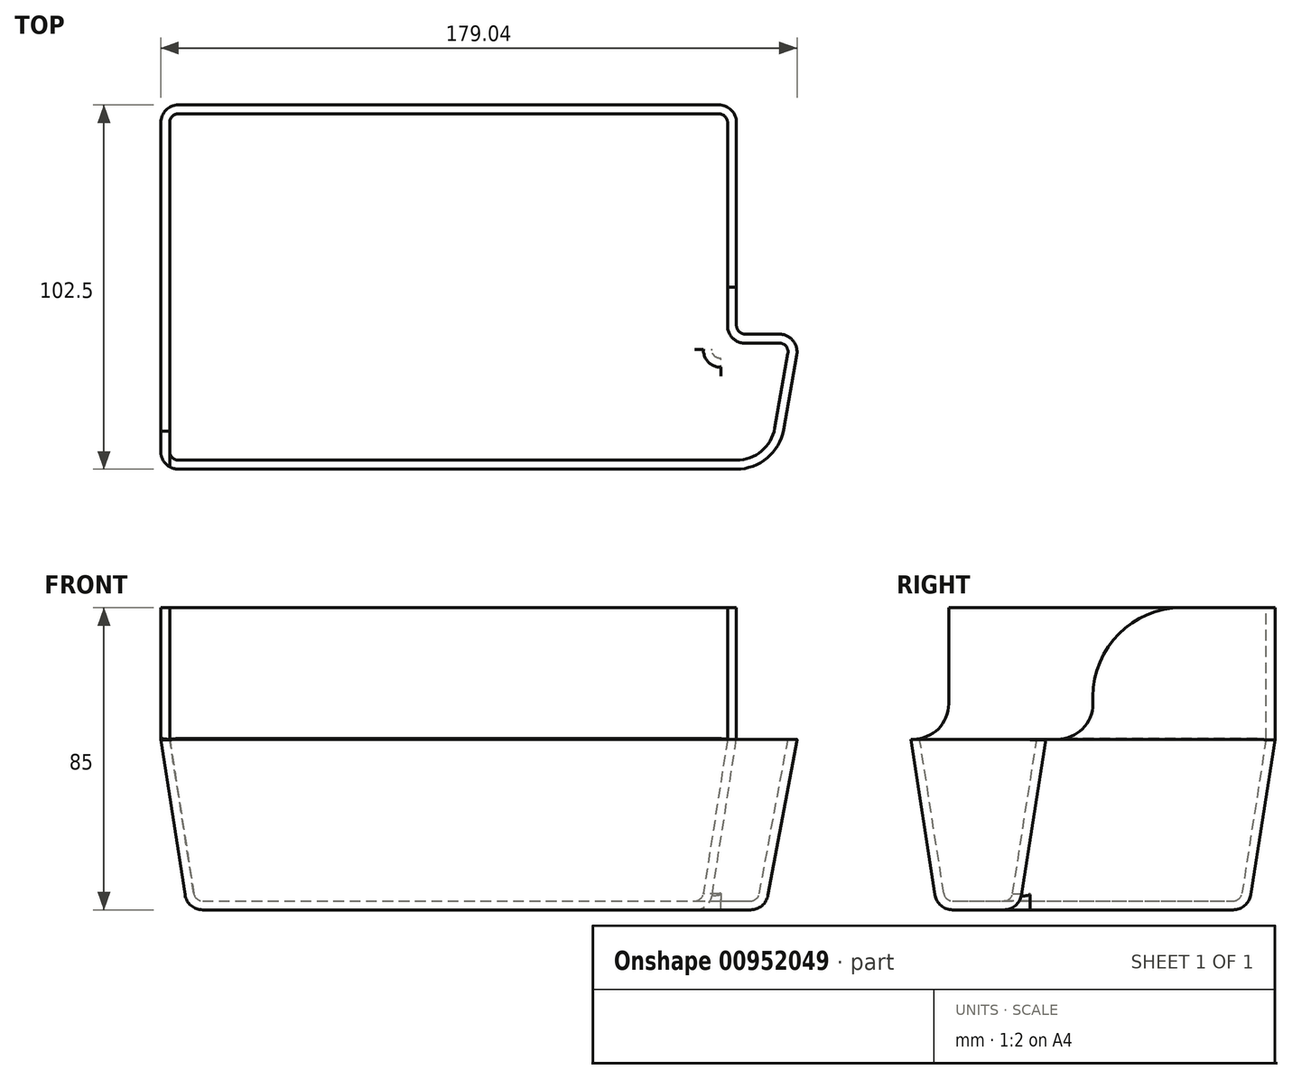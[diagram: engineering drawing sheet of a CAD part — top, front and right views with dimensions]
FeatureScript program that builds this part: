
annotation { "Feature Type Name" : "Feature", "Feature Type Description" : "" }
export const myFeature = defineFeature(function(context is Context, id is Id, definition is map)
    precondition{}
    {
        {
            var Q0;
            Q0=qCreatedBy(makeId("Top.planeOp"),FACE);
            var sketch = newSketch(context, id + "F0", { "sketchPlane" : qUnion([Q0])});
            skLineSegment(sketch, "E0.bottom", {"start": v(-81, -51.25) * mm, "end": v(81, -51.25) * mm});
            skLineSegment(sketch, "E0.top", {"start": v(-81, 51.25) * mm, "end": v(81, 51.25) * mm});
            skLineSegment(sketch, "E0.left", {"start": v(-81, -51.25) * mm, "end": v(-81, 51.25) * mm});
            skLineSegment(sketch, "E0.right", {"start": v(81, -13.25) * mm, "end": v(81, 51.25) * mm});
            skPoint(sketch, "E0.middle", {"position": v(0, 0) * mm});
            skLineSegment(sketch, "E1", {"start": v(81, -13.25) * mm, "end": v(99, -13.25) * mm});
            skLineSegment(sketch, "E2", {"start": v(99, -13.25) * mm, "end": v(94.26, -40.12) * mm});
            skArc(sketch, "E3", {"start": v(81, -51.25) * mm, "mid": v(89.66, -48.1) * mm, "end": v(94.26, -40.12) * mm});
            skSolve(sketch);
        }
        {
            var Q0;
            Q0 = qSketchRegion(id + "F0", true);
            extrude(context, id + "F1", {"entities" : qUnion([Q0]), "depth" : 85 * mm, "offsetDistance" : 25 * mm});
        }
        {
            var Q0;
            Q0=makeQuery(id+"F1.opExtrude","CAP_EDGE",EDGE,{"disambiguationData":[OSD([sQuery(id+"F0.wireOp",EDGE,"E0.bottom")])],"isStart":true});
            var Q1;
            Q1=makeQuery(id+"F1.opExtrude","CAP_EDGE",EDGE,{"disambiguationData":[OSD([sQuery(id+"F0.wireOp",EDGE,"E1")])],"isStart":true});
            var Q2;
            Q2=makeQuery(id+"F1.opExtrude","CAP_EDGE",EDGE,{"disambiguationData":[OSD([sQuery(id+"F0.wireOp",EDGE,"E0.right")])],"isStart":true});
            var Q3;
            Q3=makeQuery(id+"F1.opExtrude","CAP_EDGE",EDGE,{"disambiguationData":[OSD([sQuery(id+"F0.wireOp",EDGE,"E0.top")])],"isStart":true});
            var Q4;
            Q4=makeQuery(id+"F1.opExtrude","CAP_EDGE",EDGE,{"disambiguationData":[OSD([sQuery(id+"F0.wireOp",EDGE,"E0.left")])],"isStart":true});
            chamfer(context, id + "F2", {"entities" : qUnion([Q0, Q1, Q2, Q3, Q4]), "chamferType" : ChamferType.TWO_OFFSETS, "width1" : 48 * mm, "oppositeDirection" : false, "width2" : 7.5 * mm, "tangentPropagation" : true});
        }
        {
            var Q0;
            Q0=makeQuery(id+"F2.opChamfer","BLEND_EDGE",EDGE,{"blendedFrom":[makeQuery(id+"F1.opExtrude","CAP_EDGE",EDGE,{"disambiguationData":[OSD([sQuery(id+"F0.wireOp",EDGE,"E1")])],"isStart":true}),makeQuery(id+"F1.opExtrude","CAP_EDGE",EDGE,{"disambiguationData":[OSD([sQuery(id+"F0.wireOp",EDGE,"E2")])],"isStart":true})],"blendedInto":[]});
            var Q1;
            Q1=makeQuery(id+"F1.opExtrude","SWEPT_EDGE",EDGE,{"disambiguationData":[OSD([sQuery(id+"F0.wireOp",EDGE,"E1"),sQuery(id+"F0.wireOp",EDGE,"E2")])]});
            fillet(context, id + "F3", {"entities" : qUnion([Q0, Q1]), "radius" : 5 * mm, "tangentPropagation" : true, "allowEdgeOverflow" : false});
        }
        {
            var Q0;
            Q0=makeQuery(id+"F2.opChamfer","BLEND_EDGE",EDGE,{"blendedFrom":[makeQuery(id+"F1.opExtrude","CAP_EDGE",EDGE,{"disambiguationData":[OSD([sQuery(id+"F0.wireOp",EDGE,"E0.right")])],"isStart":true}),makeQuery(id+"F1.opExtrude","CAP_EDGE",EDGE,{"disambiguationData":[OSD([sQuery(id+"F0.wireOp",EDGE,"E1")])],"isStart":true})],"blendedInto":[]});
            var Q1;
            Q1=makeQuery(id+"F1.opExtrude","SWEPT_EDGE",EDGE,{"disambiguationData":[OSD([sQuery(id+"F0.wireOp",EDGE,"E0.right"),sQuery(id+"F0.wireOp",EDGE,"E1")])]});
            fillet(context, id + "F4", {"entities" : qUnion([Q0, Q1]), "radius" : 2.5 * mm, "tangentPropagation" : true, "allowEdgeOverflow" : false});
        }
        {
            var Q0;
            Q0=makeQuery(id+"F1.opExtrude","SWEPT_EDGE",EDGE,{"disambiguationData":[OSD([sQuery(id+"F0.wireOp",EDGE,"E0.bottom"),sQuery(id+"F0.wireOp",EDGE,"E0.left")])]});
            var Q1;
            Q1=makeQuery(id+"F2.opChamfer","BLEND_EDGE",EDGE,{"blendedFrom":[makeQuery(id+"F1.opExtrude","CAP_EDGE",EDGE,{"disambiguationData":[OSD([sQuery(id+"F0.wireOp",EDGE,"E0.bottom")])],"isStart":true}),makeQuery(id+"F1.opExtrude","CAP_EDGE",EDGE,{"disambiguationData":[OSD([sQuery(id+"F0.wireOp",EDGE,"E0.left")])],"isStart":true})],"blendedInto":[]});
            var Q2;
            Q2=makeQuery(id+"F1.opExtrude","SWEPT_EDGE",EDGE,{"disambiguationData":[OSD([sQuery(id+"F0.wireOp",EDGE,"E0.top"),sQuery(id+"F0.wireOp",EDGE,"E0.left")])]});
            var Q3;
            Q3=makeQuery(id+"F2.opChamfer","BLEND_EDGE",EDGE,{"blendedFrom":[makeQuery(id+"F1.opExtrude","CAP_EDGE",EDGE,{"disambiguationData":[OSD([sQuery(id+"F0.wireOp",EDGE,"E0.top")])],"isStart":true}),makeQuery(id+"F1.opExtrude","CAP_EDGE",EDGE,{"disambiguationData":[OSD([sQuery(id+"F0.wireOp",EDGE,"E0.left")])],"isStart":true})],"blendedInto":[]});
            var Q4;
            Q4=makeQuery(id+"F2.opChamfer","BLEND_EDGE",EDGE,{"blendedFrom":[makeQuery(id+"F1.opExtrude","CAP_EDGE",EDGE,{"disambiguationData":[OSD([sQuery(id+"F0.wireOp",EDGE,"E0.top")])],"isStart":true}),makeQuery(id+"F1.opExtrude","CAP_EDGE",EDGE,{"disambiguationData":[OSD([sQuery(id+"F0.wireOp",EDGE,"E0.right")])],"isStart":true})],"blendedInto":[]});
            var Q5;
            Q5=makeQuery(id+"F1.opExtrude","SWEPT_EDGE",EDGE,{"disambiguationData":[OSD([sQuery(id+"F0.wireOp",EDGE,"E0.top"),sQuery(id+"F0.wireOp",EDGE,"E0.right")])]});
            fillet(context, id + "F5", {"entities" : qUnion([Q0, Q1, Q2, Q3, Q4, Q5]), "radius" : 5 * mm, "tangentPropagation" : true, "allowEdgeOverflow" : false});
        }
        {
            var Q0;
            Q0=makeQuery(id+"F1.opExtrude","CAP_FACE",FACE,{"disambiguationData":[OSD([sQuery(id+"F0.wireOp",EDGE,"E0.bottom"),sQuery(id+"F0.wireOp",EDGE,"E0.top"),sQuery(id+"F0.wireOp",EDGE,"E0.left"),sQuery(id+"F0.wireOp",EDGE,"E0.right"),sQuery(id+"F0.wireOp",EDGE,"E1"),sQuery(id+"F0.wireOp",EDGE,"E2"),sQuery(id+"F0.wireOp",EDGE,"E3")])],"isStart":true});
            fillet(context, id + "F6", {"entities" : qUnion([Q0]), "radius" : 5 * mm, "tangentPropagation" : true, "allowEdgeOverflow" : false});
        }
        {
            var Q0;
            Q0=makeQuery(id+"F1.opExtrude","CAP_FACE",FACE,{"disambiguationData":[OSD([sQuery(id+"F0.wireOp",EDGE,"E0.bottom"),sQuery(id+"F0.wireOp",EDGE,"E0.top"),sQuery(id+"F0.wireOp",EDGE,"E0.left"),sQuery(id+"F0.wireOp",EDGE,"E0.right"),sQuery(id+"F0.wireOp",EDGE,"E1"),sQuery(id+"F0.wireOp",EDGE,"E2"),sQuery(id+"F0.wireOp",EDGE,"E3")])],"isStart":false});
            shell(context, id + "F7", {"entities" : qUnion([Q0]), "thickness" : 2.5 * mm});
        }
        {
            var Q0;
            Q0=qCreatedBy(makeId("Front.planeOp"),FACE);
            var sketch = newSketch(context, id + "F8", { "sketchPlane" : qUnion([Q0])});
            skLineSegment(sketch, "E4.bottom", {"start": v(-78.5, 48) * mm, "end": v(117.02, 48) * mm});
            skLineSegment(sketch, "E4.top", {"start": v(-78.5, 92.35) * mm, "end": v(117.02, 92.35) * mm});
            skLineSegment(sketch, "E4.left", {"start": v(-78.5, 48) * mm, "end": v(-78.5, 92.35) * mm});
            skLineSegment(sketch, "E4.right", {"start": v(117.02, 48) * mm, "end": v(117.02, 92.35) * mm});
            skSolve(sketch);
        }
        {
            var Q0;
            Q0 = qSketchRegion(id + "F8", true);
            extrude(context, id + "F9", {"entities" : qUnion([Q0]), "operationType" : NewBodyOperationType.REMOVE, "depth" : 167 * mm, "offsetDistance" : 25 * mm});
        }
        {
            var Q0;
            {var subQ0=sQuery(id+"F0.wireOp",EDGE,"E0.left");Q0=makeQuery(id+"F9.boolean.opBoolean","MERGE",FACE,{"derivedFrom":[makeQuery(id+"F7.opShell","OFFSET_FACE",FACE,{"disambiguationData":[OSD([subQ0]),TDD([makeQuery(id+"F1.opExtrude","SWEPT_FACE",FACE,{"disambiguationData":[OSD([subQ0])]})])]})],"fromTools":[makeQuery(id+"F9.opExtrude","SWEPT_FACE",FACE,{"disambiguationData":[OSD([sQuery(id+"F8.wireOp",EDGE,"E4.left")])]})]});}
            var sketch = newSketch(context, id + "F10", { "sketchPlane" : qUnion([Q0])});
            skLineSegment(sketch, "E5.bottom", {"start": v(-50.58, 48) * mm, "end": v(-40.58, 48) * mm});
            skLineSegment(sketch, "E5.top", {"start": v(-50.58, 85) * mm, "end": v(-40.58, 85) * mm});
            skLineSegment(sketch, "E5.left", {"start": v(-50.58, 48) * mm, "end": v(-50.58, 85) * mm});
            skLineSegment(sketch, "E5.right", {"start": v(-40.58, 48) * mm, "end": v(-40.58, 85) * mm});
            skSolve(sketch);
        }
        {
            var Q0;
            Q0 = qSketchRegion(id + "F10", true);
            extrude(context, id + "F11", {"entities" : qUnion([Q0]), "operationType" : NewBodyOperationType.REMOVE, "oppositeDirection" : true, "depth" : 25 * mm, "offsetDistance" : 25 * mm});
        }
        {
            var Q0;
            Q0=makeQuery(id+"F11.boolean.opBoolean","COPY",EDGE,{"derivedFrom":makeQuery(id+"F11.opExtrude","SWEPT_EDGE",EDGE,{"disambiguationData":[OSD([sQuery(id+"F0.wireOp",EDGE,"E0.bottom"),sQuery(id+"F0.wireOp",EDGE,"E0.top"),sQuery(id+"F0.wireOp",EDGE,"E0.left"),sQuery(id+"F0.wireOp",EDGE,"E0.right"),sQuery(id+"F0.wireOp",EDGE,"E1"),sQuery(id+"F0.wireOp",EDGE,"E2"),sQuery(id+"F0.wireOp",EDGE,"E3"),sQuery(id+"F8.wireOp",EDGE,"E4.left"),sQuery(id+"F10.wireOp",EDGE,"E5.top"),sQuery(id+"F10.wireOp",EDGE,"E5.right")])]})});
            var Q1;
            Q1=makeQuery(id+"F9.boolean.opBoolean","INTERSECT",EDGE,{"derivedFrom":[makeQuery(id+"F1.opExtrude","CAP_FACE",FACE,{"disambiguationData":[OSD([sQuery(id+"F0.wireOp",EDGE,"E0.bottom"),sQuery(id+"F0.wireOp",EDGE,"E0.top"),sQuery(id+"F0.wireOp",EDGE,"E0.left"),sQuery(id+"F0.wireOp",EDGE,"E0.right"),sQuery(id+"F0.wireOp",EDGE,"E1"),sQuery(id+"F0.wireOp",EDGE,"E2"),sQuery(id+"F0.wireOp",EDGE,"E3")])],"isStart":false}),makeQuery(id+"F9.opExtrude","CAP_FACE",FACE,{"disambiguationData":[OSD([sQuery(id+"F8.wireOp",EDGE,"E4.bottom"),sQuery(id+"F8.wireOp",EDGE,"E4.top"),sQuery(id+"F8.wireOp",EDGE,"E4.left"),sQuery(id+"F8.wireOp",EDGE,"E4.right")])],"isStart":true})]});
            fillet(context, id + "F12", {"entities" : qUnion([Q0, Q1]), "radius" : 25 * mm, "tangentPropagation" : true, "allowEdgeOverflow" : false});
        }
        {
            var Q0;
            Q0=makeQuery(id+"F11.boolean.opBoolean","COPY",EDGE,{"derivedFrom":makeQuery(id+"F11.opExtrude","SWEPT_EDGE",EDGE,{"disambiguationData":[OSD([sQuery(id+"F8.wireOp",EDGE,"E4.bottom"),sQuery(id+"F8.wireOp",EDGE,"E4.left"),sQuery(id+"F10.wireOp",EDGE,"E5.bottom"),sQuery(id+"F10.wireOp",EDGE,"E5.right")])]})});
            var Q1;
            {var subQ0=sQuery(id+"F0.wireOp",EDGE,"E0.right");var subQ2=sQuery(id+"F8.wireOp",EDGE,"E4.bottom");Q1=makeQuery(id+"F9.boolean.opBoolean","COPY",EDGE,{"disambiguationData":[TD([makeQuery(id+"F1.opExtrude","SWEPT_FACE",FACE,{"disambiguationData":[OSD([subQ0])]})])],"derivedFrom":makeQuery(id+"F9.opExtrude","CAP_EDGE",EDGE,{"disambiguationData":[OSD([subQ2])],"isStart":true})});}
            fillet(context, id + "F13", {"entities" : qUnion([Q0, Q1]), "radius" : 10 * mm, "tangentPropagation" : true, "allowEdgeOverflow" : false});
        }
    });
